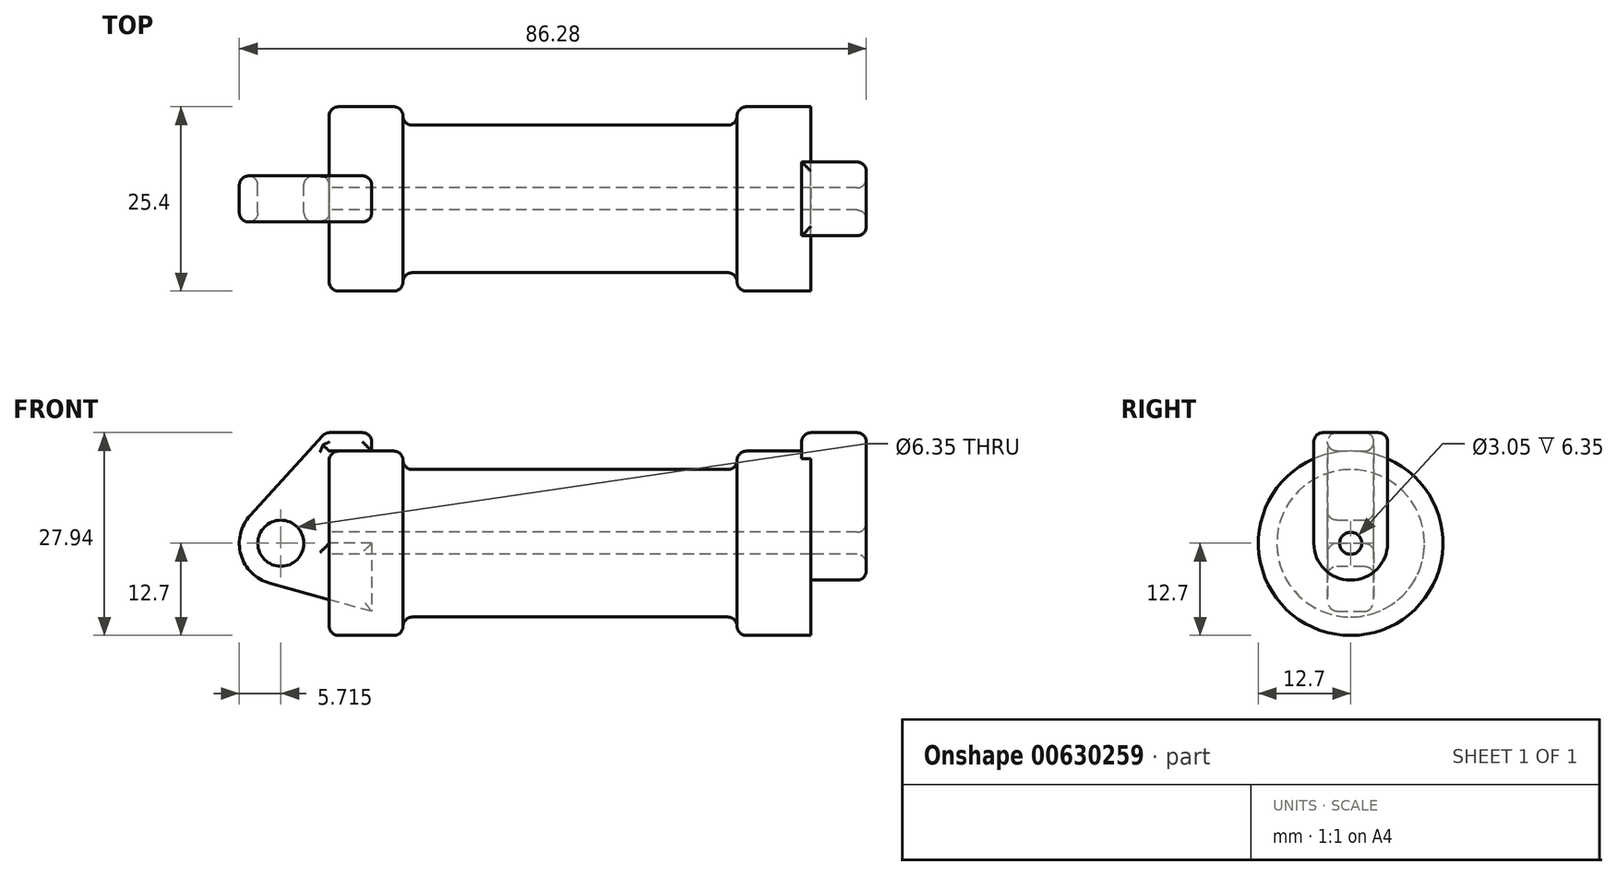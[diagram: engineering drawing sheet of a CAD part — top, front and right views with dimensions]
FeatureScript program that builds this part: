
annotation { "Feature Type Name" : "Feature", "Feature Type Description" : "" }
export const myFeature = defineFeature(function(context is Context, id is Id, definition is map)
    precondition{}
    {
        {
            var Q0;
            Q0=qCreatedBy(makeId("Front.planeOp"),FACE);
            var sketch = newSketch(context, id + "F0", { "sketchPlane" : qUnion([Q0])});
            skLineSegment(sketch, "E0", {"start": v(0, 0) * mm, "end": v(0, 12.7) * mm});
            skLineSegment(sketch, "E1", {"start": v(0, 12.7) * mm, "end": v(10.16, 12.7) * mm});
            skLineSegment(sketch, "E2", {"start": v(10.16, 12.7) * mm, "end": v(10.16, 10.16) * mm});
            skLineSegment(sketch, "E3", {"start": v(10.16, 10.16) * mm, "end": v(56.13, 10.16) * mm});
            skLineSegment(sketch, "E4", {"start": v(56.13, 10.16) * mm, "end": v(56.13, 12.7) * mm});
            skLineSegment(sketch, "E5", {"start": v(56.13, 12.7) * mm, "end": v(66.3, 12.7) * mm});
            skLineSegment(sketch, "E6", {"start": v(66.3, 12.7) * mm, "end": v(66.3, 0) * mm});
            skLineSegment(sketch, "E7", {"start": v(66.3, 0) * mm, "end": v(0, 0) * mm});
            skLineSegment(sketch, "E8", {"start": v(5.84, 15.24) * mm, "end": v(-0.5, 15.24) * mm});
            skLineSegment(sketch, "E9", {"start": v(-0.5, 15.24) * mm, "end": v(-10.88, 3.85) * mm});
            skLineSegment(sketch, "E10", {"start": v(0, 0) * mm, "end": v(-6.65, 0) * mm});
            skCircle(sketch, "E11", {"center": v(-6.65, 0) * mm, "radius": 5.72 * mm});
            skCircle(sketch, "E12", {"center": v(-6.65, 0) * mm, "radius": 3.18 * mm});
            skLineSegment(sketch, "E13", {"start": v(5.84, 15.24) * mm, "end": v(5.84, -9.4) * mm});
            skLineSegment(sketch, "E14", {"start": v(5.84, -9.4) * mm, "end": v(-8.18, -5.5) * mm});
            skSolve(sketch);
        }
        {
            var Q0;
            {var subQ0=sQuery(id+"F0.wireOp",EDGE,"E0");Q0=makeQuery(id+"F0.imprint","IMPRINT",FACE,{"disambiguationData":[TD([[makeQuery(id+"F0.imprint","IMPRINT",EDGE,{"derivedFrom":subQ0}),-1.0]])]});}
            var Q1;
            {var subQ0=sQuery(id+"F0.wireOp",EDGE,"E2");Q1=makeQuery(id+"F0.imprint","IMPRINT",FACE,{"disambiguationData":[TD([[makeQuery(id+"F0.imprint","IMPRINT",EDGE,{"derivedFrom":subQ0}),-1.0]])]});}
            var Q2;
            Q2=sQuery(id+"F0.wireOp",EDGE,"E7");
            revolve(context, id + "F1", {"entities" : qUnion([Q0, Q1]), "axis" : qUnion([Q2]), "revolveType" : RevolveType.FULL});
        }
        {
            var Q0;
            {var subQ1=sQuery(id+"F0.wireOp",EDGE,"E0");Q0=makeQuery(id+"F0.imprint","IMPRINT",FACE,{"disambiguationData":[TD([[makeQuery(id+"F0.imprint","IMPRINT",EDGE,{"derivedFrom":subQ1}),1.0]])]});}
            var Q1;
            {var subQ0=sQuery(id+"F0.wireOp",EDGE,"E14");Q1=makeQuery(id+"F0.imprint","IMPRINT",FACE,{"disambiguationData":[TD([[makeQuery(id+"F0.imprint","IMPRINT",EDGE,{"derivedFrom":subQ0}),-1.0]])]});}
            var Q2;
            {var subQ5=sQuery(id+"F0.wireOp",EDGE,"E12");Q2=makeQuery(id+"F0.imprint","IMPRINT",FACE,{"disambiguationData":[TD([[makeQuery(id+"F0.imprint","IMPRINT",EDGE,{"derivedFrom":subQ5}),-1.0]])]});}
            extrude(context, id + "F2", {"entities" : qUnion([Q0, Q1, Q2]), "depth" : 6.35 * mm, "offsetDistance" : 25.4 * mm, "symmetric" : true});
        }
        {
            var Q0;
            Q0=makeQuery(id+"F1.opRevolve","SWEPT_FACE",FACE,{"disambiguationData":[OSD([sQuery(id+"F0.wireOp",EDGE,"E6")])]});
            var sketch = newSketch(context, id + "F3", { "sketchPlane" : qUnion([Q0])});
            skCircle(sketch, "E15", {"center": v(0, 0) * mm, "radius": 1.52 * mm});
            skCircle(sketch, "E16", {"center": v(0, 0) * mm, "radius": 5.08 * mm});
            skLineSegment(sketch, "E17", {"start": v(5.08, 0) * mm, "end": v(5.08, 15.24) * mm});
            skLineSegment(sketch, "E18", {"start": v(-5.08, 0) * mm, "end": v(-5.08, 15.24) * mm});
            skLineSegment(sketch, "E19", {"start": v(-5.08, 15.24) * mm, "end": v(5.08, 15.24) * mm});
            skSolve(sketch);
        }
        {
            var Q0;
            {var subQ0=sQuery(id+"F3.wireOp",EDGE,"E19");Q0=makeQuery(id+"F3.imprint","IMPRINT",FACE,{"disambiguationData":[TD([[makeQuery(id+"F3.imprint","IMPRINT",EDGE,{"derivedFrom":subQ0}),-1.0]])]});}
            var Q1;
            {var subQ0=sQuery(id+"F3.wireOp",EDGE,"E17");var subQ1=sQuery(id+"F3.wireOp",EDGE,"E16");var subQ2=makeQuery(id+"F3.imprint","INTERSECT",VERTEX,{"derivedFrom":[subQ1,subQ0]});Q1=makeQuery(id+"F3.imprint","IMPRINT",FACE,{"disambiguationData":[TD([[makeQuery(id+"F3.imprint","IMPRINT",EDGE,{"disambiguationData":[TD([[subQ2,-1.0]])],"derivedFrom":subQ1}),-1.0]])]});}
            var Q2;
            Q2=makeQuery(id+"F3.imprint","IMPRINT",FACE,{"disambiguationData":[TD([[makeQuery(id+"F3.imprint","IMPRINT",EDGE,{"derivedFrom":sQuery(id+"F3.wireOp",EDGE,"E15")}),-1.0]])]});
            extrude(context, id + "F4", {"entities" : qUnion([Q0, Q1, Q2]), "operationType" : NewBodyOperationType.ADD, "depth" : 7.62 * mm, "offsetDistance" : 25.4 * mm});
        }
        {
            var Q0;
            Q0=makeQuery(id+"F4.opExtrude","CAP_FACE",FACE,{"disambiguationData":[OSD([sQuery(id+"F3.wireOp",EDGE,"E15"),sQuery(id+"F3.wireOp",EDGE,"E16"),sQuery(id+"F3.wireOp",EDGE,"E17"),sQuery(id+"F3.wireOp",EDGE,"E18"),sQuery(id+"F3.wireOp",EDGE,"E19")])],"isStart":true});
            extrude(context, id + "F5", {"entities" : qUnion([Q0]), "operationType" : NewBodyOperationType.ADD, "depth" : 1.27 * mm, "offsetDistance" : 25.4 * mm});
        }
        {
            var Q0;
            Q0=makeQuery(id+"F4.boolean.opBoolean","SPLIT",FACE,{"disambiguationData":[TD([makeQuery(id+"F4.opExtrude","SWEPT_FACE",FACE,{"disambiguationData":[OSD([sQuery(id+"F3.wireOp",EDGE,"E15")])]})])],"derivedFrom":makeQuery(id+"F1.opRevolve","SWEPT_FACE",FACE,{"disambiguationData":[OSD([sQuery(id+"F0.wireOp",EDGE,"E6")])]})});
            var Q1;
            Q1=sQuery(id+"F0.wireOp",EDGE,"E7");
            sweep(context, id + "F6", {"profiles" : qUnion([Q0]), "path" : qUnion([Q1])});
        }
        {
            var Q0;
            {var subQ0=sQuery(id+"F3.wireOp",EDGE,"E19");Q0=makeQuery(id+"F5.boolean.opBoolean","MERGE",FACE,{"derivedFrom":[makeQuery(id+"F4.opExtrude","SWEPT_FACE",FACE,{"disambiguationData":[OSD([subQ0])]}),makeQuery(id+"F5.opExtrude","SWEPT_FACE",FACE,{"disambiguationData":[OSD([subQ0])]})]});}
            var sketch = newSketch(context, id + "F7", { "sketchPlane" : qUnion([Q0])});
            skCircle(sketch, "E20", {"center": v(69.47, 0) * mm, "radius": 1.52 * mm});
            skPoint(sketch, "E20.centerSnap0", {"position": v(73.91, 0) * mm});
            skPoint(sketch, "E20.centerSnap1", {"position": v(69.47, 5.08) * mm});
            skSolve(sketch);
        }
        {
            var Q0;
            Q0=makeQuery(id+"F2.opExtrude","SWEPT_FACE",FACE,{"disambiguationData":[OSD([sQuery(id+"F0.wireOp",EDGE,"E8")])]});
            var sketch = newSketch(context, id + "F8", { "sketchPlane" : qUnion([Q0])});
            skCircle(sketch, "E21", {"center": v(2.67, 0) * mm, "radius": 1.52 * mm});
            skPoint(sketch, "E21.centerSnap0", {"position": v(2.67, 3.18) * mm});
            skPoint(sketch, "E21.centerSnap1", {"position": v(5.84, 0) * mm});
            skSolve(sketch);
        }
        {
            var Q0;
            Q0=sQuery(id+"F8.wireOp",EDGE,"E21");
            extrude(context, id + "F9", {"bodyType" : ToolBodyType.SURFACE, "surfaceEntities" : qUnion([Q0]), "oppositeDirection" : true, "depth" : 17.78 * mm, "offsetDistance" : 25.4 * mm});
        }
        {
            var Q0;
            Q0=sQuery(id+"F7.wireOp",EDGE,"E20");
            extrude(context, id + "F10", {"bodyType" : ToolBodyType.SURFACE, "surfaceEntities" : qUnion([Q0]), "oppositeDirection" : true, "depth" : 10.4 * mm, "offsetDistance" : 25.4 * mm});
        }
        {
            var Q0;
            Q0=makeQuery(id+"F1.opRevolve","SWEPT_EDGE",EDGE,{"disambiguationData":[OSD([sQuery(id+"F0.wireOp",EDGE,"E4"),sQuery(id+"F0.wireOp",EDGE,"E5")])]});
            var Q1;
            Q1=makeQuery(id+"F1.opRevolve","SWEPT_EDGE",EDGE,{"disambiguationData":[OSD([sQuery(id+"F0.wireOp",EDGE,"E3"),sQuery(id+"F0.wireOp",EDGE,"E4")])]});
            var Q2;
            Q2=makeQuery(id+"F1.opRevolve","SWEPT_EDGE",EDGE,{"disambiguationData":[OSD([sQuery(id+"F0.wireOp",EDGE,"E1"),sQuery(id+"F0.wireOp",EDGE,"E2")])]});
            var Q3;
            Q3=makeQuery(id+"F1.opRevolve","SWEPT_EDGE",EDGE,{"disambiguationData":[OSD([sQuery(id+"F0.wireOp",EDGE,"E2"),sQuery(id+"F0.wireOp",EDGE,"E3")])]});
            var Q4;
            Q4=makeQuery(id+"F5.opExtrude","CAP_EDGE",EDGE,{"disambiguationData":[OSD([sQuery(id+"F0.wireOp",EDGE,"E5"),sQuery(id+"F0.wireOp",EDGE,"E6")])],"isStart":false});
            var Q5;
            {var subQ0=sQuery(id+"F3.wireOp",EDGE,"E18");var subQ1=sQuery(id+"F3.wireOp",EDGE,"E19");var subQ2=sQuery(id+"F3.wireOp",EDGE,"E17");var subQ3=sQuery(id+"F3.wireOp",EDGE,"E16");var subQ4=sQuery(id+"F3.wireOp",EDGE,"E15");var subQ5=sQuery(id+"F0.wireOp",EDGE,"E6");var subQ6=sQuery(id+"F0.wireOp",EDGE,"E5");Q5=makeQuery(id+"F5.opExtrude","SWEPT_EDGE",EDGE,{"disambiguationData":[OSD([subQ6,subQ5,subQ4,subQ3,subQ2,subQ0,subQ1]),TDD([makeQuery(id+"F4.boolean.opBoolean","TWEAK_VERTEX",VERTEX,{"derivedFrom":[makeQuery(id+"F1.opRevolve","SWEPT_FACE",FACE,{"disambiguationData":[OSD([subQ6])]}),makeQuery(id+"F1.opRevolve","SWEPT_FACE",FACE,{"disambiguationData":[OSD([subQ5])]}),makeQuery(id+"F4.opExtrude","CAP_FACE",FACE,{"disambiguationData":[OSD([subQ4,subQ3,subQ2,subQ0,subQ1])],"isStart":true}),makeQuery(id+"F4.opExtrude","SWEPT_FACE",FACE,{"disambiguationData":[OSD([subQ0])]})]})])]});}
            var Q6;
            {var subQ0=sQuery(id+"F3.wireOp",EDGE,"E18");Q6=makeQuery(id+"F4.boolean.opBoolean","SPLIT",EDGE,{"disambiguationData":[topologyDisambiguationEdgeConnected([makeQuery(id+"F1.opRevolve","SWEPT_FACE",FACE,{"disambiguationData":[OSD([sQuery(id+"F0.wireOp",EDGE,"E6")])]})])],"derivedFrom":makeQuery(id+"F4.opExtrude","CAP_EDGE",EDGE,{"disambiguationData":[OSD([subQ0])],"isStart":true})});}
            var Q7;
            {var subQ0=sQuery(id+"F3.wireOp",EDGE,"E17");var subQ1=sQuery(id+"F3.wireOp",EDGE,"E19");var subQ2=sQuery(id+"F3.wireOp",EDGE,"E18");var subQ3=sQuery(id+"F3.wireOp",EDGE,"E16");var subQ4=sQuery(id+"F3.wireOp",EDGE,"E15");var subQ5=sQuery(id+"F0.wireOp",EDGE,"E6");var subQ6=sQuery(id+"F0.wireOp",EDGE,"E5");Q7=makeQuery(id+"F5.opExtrude","SWEPT_EDGE",EDGE,{"disambiguationData":[OSD([subQ6,subQ5,subQ4,subQ3,subQ0,subQ2,subQ1]),TDD([makeQuery(id+"F4.boolean.opBoolean","TWEAK_VERTEX",VERTEX,{"derivedFrom":[makeQuery(id+"F1.opRevolve","SWEPT_FACE",FACE,{"disambiguationData":[OSD([subQ6])]}),makeQuery(id+"F1.opRevolve","SWEPT_FACE",FACE,{"disambiguationData":[OSD([subQ5])]}),makeQuery(id+"F4.opExtrude","CAP_FACE",FACE,{"disambiguationData":[OSD([subQ4,subQ3,subQ0,subQ2,subQ1])],"isStart":true}),makeQuery(id+"F4.opExtrude","SWEPT_FACE",FACE,{"disambiguationData":[OSD([subQ0])]})]})])]});}
            var Q8;
            Q8=makeQuery(id+"F4.opExtrude","CAP_FACE",FACE,{"disambiguationData":[OSD([sQuery(id+"F3.wireOp",EDGE,"E15"),sQuery(id+"F3.wireOp",EDGE,"E16"),sQuery(id+"F3.wireOp",EDGE,"E17"),sQuery(id+"F3.wireOp",EDGE,"E18"),sQuery(id+"F3.wireOp",EDGE,"E19")])],"isStart":false});
            var Q9;
            {var subQ0=sQuery(id+"F3.wireOp",EDGE,"E19");Q9=makeQuery(id+"F5.boolean.opBoolean","MERGE",FACE,{"derivedFrom":[makeQuery(id+"F4.opExtrude","SWEPT_FACE",FACE,{"disambiguationData":[OSD([subQ0])]}),makeQuery(id+"F5.opExtrude","SWEPT_FACE",FACE,{"disambiguationData":[OSD([subQ0])]})]});}
            fillet(context, id + "F11", {"entities" : qUnion([Q0, Q1, Q2, Q3, Q4, Q5, Q6, Q7, Q8, Q9]), "radius" : 1.27 * mm, "tangentPropagation" : true, "allowEdgeOverflow" : false});
        }
        {
            var Q0;
            Q0=makeQuery(id+"F2.opExtrude","CAP_FACE",FACE,{"disambiguationData":[OSD([sQuery(id+"F0.wireOp",EDGE,"E0"),sQuery(id+"F0.wireOp",EDGE,"E1"),sQuery(id+"F0.wireOp",EDGE,"E7"),sQuery(id+"F0.wireOp",EDGE,"E8"),sQuery(id+"F0.wireOp",EDGE,"E9"),sQuery(id+"F0.wireOp",EDGE,"E11"),sQuery(id+"F0.wireOp",EDGE,"E12"),sQuery(id+"F0.wireOp",EDGE,"E13"),sQuery(id+"F0.wireOp",EDGE,"E14")])],"isStart":false});
            var Q1;
            Q1=makeQuery(id+"F2.opExtrude","CAP_FACE",FACE,{"disambiguationData":[OSD([sQuery(id+"F0.wireOp",EDGE,"E0"),sQuery(id+"F0.wireOp",EDGE,"E1"),sQuery(id+"F0.wireOp",EDGE,"E7"),sQuery(id+"F0.wireOp",EDGE,"E8"),sQuery(id+"F0.wireOp",EDGE,"E9"),sQuery(id+"F0.wireOp",EDGE,"E11"),sQuery(id+"F0.wireOp",EDGE,"E12"),sQuery(id+"F0.wireOp",EDGE,"E13"),sQuery(id+"F0.wireOp",EDGE,"E14")])],"isStart":true});
            var Q2;
            Q2=makeQuery(id+"F2.opExtrude","SWEPT_FACE",FACE,{"disambiguationData":[OSD([sQuery(id+"F0.wireOp",EDGE,"E8")])]});
            var Q3;
            Q3=makeQuery(id+"F1.opRevolve","SWEPT_FACE",FACE,{"disambiguationData":[OSD([sQuery(id+"F0.wireOp",EDGE,"E0")])]});
            fillet(context, id + "F12", {"entities" : qUnion([Q0, Q1, Q2, Q3]), "radius" : 1.27 * mm, "allowEdgeOverflow" : false});
        }
    });
